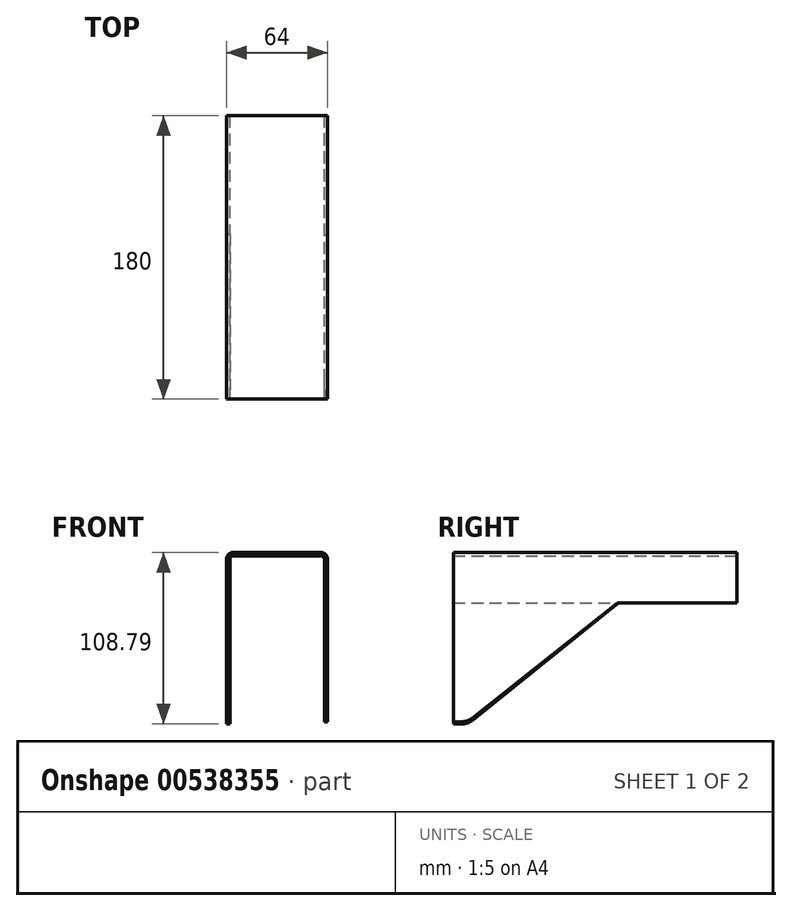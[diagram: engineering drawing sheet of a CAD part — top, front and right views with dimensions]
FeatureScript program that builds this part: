
annotation { "Feature Type Name" : "Feature", "Feature Type Description" : "" }
export const myFeature = defineFeature(function(context is Context, id is Id, definition is map)
    precondition{}
    {
        {
            var Q0;
            Q0=qCreatedBy(makeId("Front.planeOp"),FACE);
            var sketch = newSketch(context, id + "F0", { "sketchPlane" : qUnion([Q0])});
            skLineSegment(sketch, "E0", {"start": v(0, 0) * mm, "end": v(0, 28) * mm});
            skLineSegment(sketch, "E1", {"start": v(2, 30) * mm, "end": v(58, 30) * mm});
            skLineSegment(sketch, "E2", {"start": v(60, 28) * mm, "end": v(60, 0) * mm});
            skPoint(sketch, "E3.visualSharp", {"position": v(0, 30) * mm});
            skArc(sketch, "E3.filletArc", {"start": v(2, 30) * mm, "mid": v(0.59, 29.41) * mm, "end": v(0, 28) * mm});
            skPoint(sketch, "E4.visualSharp", {"position": v(60, 30) * mm});
            skArc(sketch, "E4.filletArc", {"start": v(60, 28) * mm, "mid": v(59.41, 29.41) * mm, "end": v(58, 30) * mm});
            skLineSegment(sketch, "E5", {"start": v(0, 0) * mm, "end": v(-2, 0) * mm});
            skLineSegment(sketch, "E6", {"start": v(-2, 0) * mm, "end": v(-2, 28) * mm});
            skLineSegment(sketch, "E7", {"start": v(2, 32) * mm, "end": v(58, 32) * mm});
            skLineSegment(sketch, "E8", {"start": v(62, 28) * mm, "end": v(62, 0) * mm});
            skLineSegment(sketch, "E9", {"start": v(62, 0) * mm, "end": v(60, 0) * mm});
            skPoint(sketch, "E10.visualSharp", {"position": v(-2, 32) * mm});
            skArc(sketch, "E10.filletArc", {"start": v(2, 32) * mm, "mid": v(-0.83, 30.83) * mm, "end": v(-2, 28) * mm});
            skPoint(sketch, "E11.visualSharp", {"position": v(62, 32) * mm});
            skArc(sketch, "E11.filletArc", {"start": v(62, 28) * mm, "mid": v(60.83, 30.83) * mm, "end": v(58, 32) * mm});
            skSolve(sketch);
        }
        {
            var Q0;
            Q0=makeQuery(id+"F0.imprint","IMPRINT",FACE,{"disambiguationData":[TD([[makeQuery(id+"F0.imprint","IMPRINT",EDGE,{"derivedFrom":sQuery(id+"F0.wireOp",EDGE,"E0")}),1.0]])]});
            extrude(context, id + "F1", {"entities" : qUnion([Q0]), "depth" : 180 * mm, "offsetDistance" : 25 * mm});
        }
        {
            var Q0;
            Q0=makeQuery(id+"F1.opExtrude","SWEPT_FACE",FACE,{"disambiguationData":[OSD([sQuery(id+"F0.wireOp",EDGE,"E8")])]});
            var sketch = newSketch(context, id + "F2", { "sketchPlane" : qUnion([Q0])});
            skLineSegment(sketch, "E12", {"start": v(-180, 0) * mm, "end": v(-180, -75.57) * mm});
            skLineSegment(sketch, "E13", {"start": v(-168.25, -73.28) * mm, "end": v(-75.9, 0) * mm});
            skPoint(sketch, "E14.visualSharp", {"position": v(-180, -82.6) * mm});
            skLineSegment(sketch, "E15", {"start": v(-174.26, -75.45) * mm, "end": v(-180, -75.57) * mm});
            skPoint(sketch, "E16.visualSharp", {"position": v(-170.89, -75.38) * mm});
            skArc(sketch, "E16.filletArc", {"start": v(-174.26, -75.45) * mm, "mid": v(-171.07, -74.86) * mm, "end": v(-168.25, -73.28) * mm});
            skSolve(sketch);
        }
        {
            var Q0;
            {var subQ0=sQuery(id+"F2.wireOp",EDGE,"E12");Q0=makeQuery(id+"F2.imprint","IMPRINT",FACE,{"disambiguationData":[TD([[makeQuery(id+"F2.imprint","IMPRINT",EDGE,{"derivedFrom":subQ0}),1.0]])]});}
            extrude(context, id + "F3", {"entities" : qUnion([Q0]), "operationType" : NewBodyOperationType.ADD, "depth" : -2 * mm, "offsetDistance" : 25 * mm});
        }
        {
            var Q0;
            Q0=makeQuery(id+"F1.opExtrude","SWEPT_FACE",FACE,{"disambiguationData":[OSD([sQuery(id+"F0.wireOp",EDGE,"E6")])]});
            var sketch = newSketch(context, id + "F4", { "sketchPlane" : qUnion([Q0])});
            skLineSegment(sketch, "E17", {"start": v(180, 0) * mm, "end": v(180, -76.79) * mm});
            skLineSegment(sketch, "E18", {"start": v(75.11, 0) * mm, "end": v(167.98, -74.58) * mm});
            skLineSegment(sketch, "E19", {"start": v(180, 0) * mm, "end": v(180, -86.4) * mm});
            skLineSegment(sketch, "E20", {"start": v(180, -76.79) * mm, "end": v(174.24, -76.79) * mm});
            skArc(sketch, "E21.filletArc", {"start": v(167.98, -74.58) * mm, "mid": v(170.92, -76.22) * mm, "end": v(174.24, -76.79) * mm});
            skSolve(sketch);
        }
        {
            var Q0;
            {var subQ5=sQuery(id+"F4.wireOp",EDGE,"E18");Q0=makeQuery(id+"F4.imprint","IMPRINT",FACE,{"disambiguationData":[TD([[makeQuery(id+"F4.imprint","IMPRINT",EDGE,{"derivedFrom":subQ5}),1.0]])]});}
            extrude(context, id + "F5", {"entities" : qUnion([Q0]), "depth" : -2 * mm, "offsetDistance" : 25 * mm});
        }
    });
